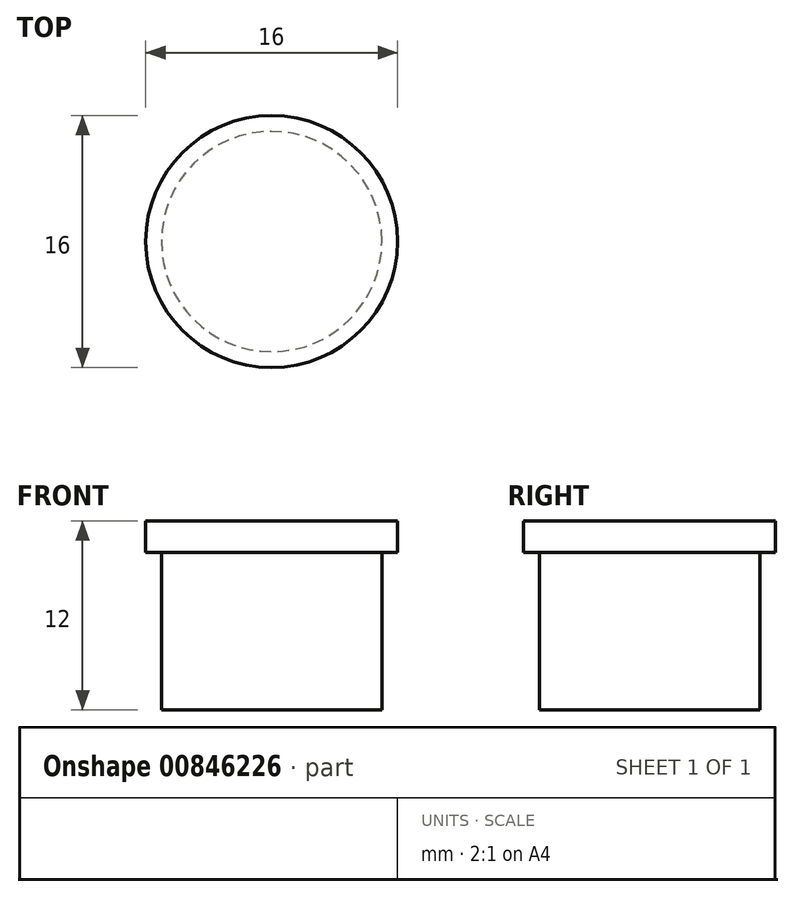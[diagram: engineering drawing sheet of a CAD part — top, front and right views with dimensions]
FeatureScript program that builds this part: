
annotation { "Feature Type Name" : "Feature", "Feature Type Description" : "" }
export const myFeature = defineFeature(function(context is Context, id is Id, definition is map)
    precondition{}
    {
        {
            var Q0;
            Q0=qCreatedBy(makeId("Front.planeOp"),FACE);
            var sketch = newSketch(context, id + "F0", { "sketchPlane" : qUnion([Q0])});
            skLineSegment(sketch, "E0", {"start": v(0, 12) * mm, "end": v(8, 12) * mm});
            skLineSegment(sketch, "E1", {"start": v(8, 12) * mm, "end": v(8, 10) * mm});
            skLineSegment(sketch, "E2", {"start": v(8, 10) * mm, "end": v(7, 10) * mm});
            skLineSegment(sketch, "E3", {"start": v(7, 10) * mm, "end": v(7, 0) * mm});
            skLineSegment(sketch, "E4", {"start": v(7, 0) * mm, "end": v(0, 0) * mm});
            skLineSegment(sketch, "E5", {"start": v(0, 0) * mm, "end": v(0, 12) * mm});
            skSolve(sketch);
        }
        {
            var Q0;
            Q0=makeQuery(id+"F0.imprint","IMPRINT",FACE,{"disambiguationData":[TD([[makeQuery(id+"F0.imprint","IMPRINT",EDGE,{"derivedFrom":sQuery(id+"F0.wireOp",EDGE,"E0")}),-1.0]])]});
            var Q1;
            Q1=sQuery(id+"F0.wireOp",EDGE,"E5");
            revolve(context, id + "F1", {"surfaceOperationType" : NewSurfaceOperationType.NEW, "entities" : qUnion([Q0]), "axis" : qUnion([Q1]), "revolveType" : RevolveType.FULL});
        }
    });
